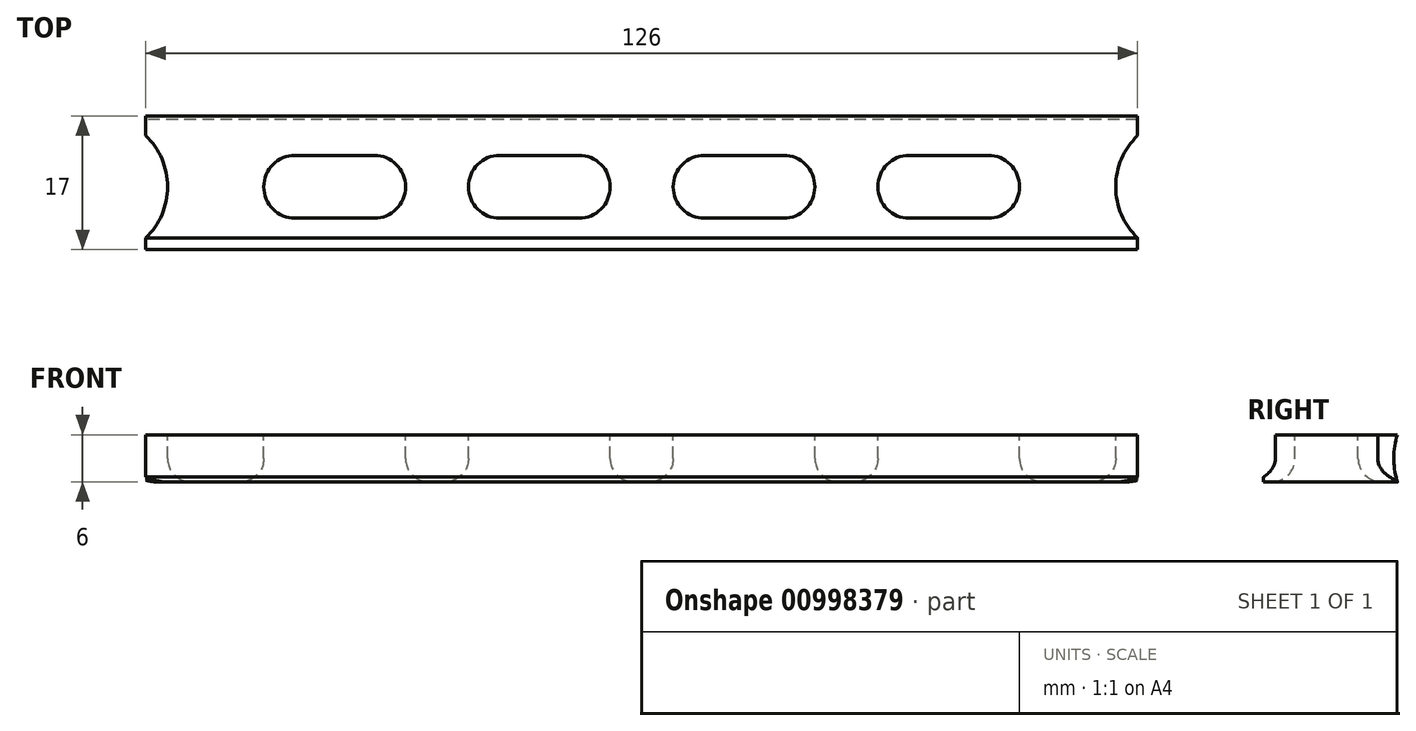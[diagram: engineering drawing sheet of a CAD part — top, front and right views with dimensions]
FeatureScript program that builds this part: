
annotation { "Feature Type Name" : "Feature", "Feature Type Description" : "" }
export const myFeature = defineFeature(function(context is Context, id is Id, definition is map)
    precondition{}
    {
        {
            var Q0;
            Q0=qCreatedBy(makeId("Right.planeOp"),FACE);
            var sketch = newSketch(context, id + "F0", { "sketchPlane" : qUnion([Q0])});
            skLineSegment(sketch, "E0.bottom", {"start": v(0, 0) * mm, "end": v(-17, 0) * mm});
            skLineSegment(sketch, "E0.top", {"start": v(0, 6) * mm, "end": v(-17, 6) * mm});
            skLineSegment(sketch, "E0.right", {"start": v(-17, 0) * mm, "end": v(-17, 6) * mm});
            skArc(sketch, "E1", {"start": v(0, 6) * mm, "mid": v(-0.46, 3) * mm, "end": v(0, 0) * mm});
            skSolve(sketch);
        }
        {
            var Q0;
            Q0=makeQuery(id+"F0.imprint","IMPRINT",FACE,{"disambiguationData":[TD([[makeQuery(id+"F0.imprint","IMPRINT",EDGE,{"derivedFrom":sQuery(id+"F0.wireOp",EDGE,"E0.bottom")}),-1.0]])]});
            extrude(context, id + "F1", {"entities" : qUnion([Q0]), "depth" : 63 * mm, "offsetDistance" : 25 * mm});
        }
        {
            var Q0;
            Q0=makeQuery(id+"F1.opExtrude","SWEPT_FACE",FACE,{"disambiguationData":[OSD([sQuery(id+"F0.wireOp",EDGE,"E0.top")])]});
            var sketch = newSketch(context, id + "F2", { "sketchPlane" : qUnion([Q0])});
            skPoint(sketch, "E2", {"position": v(63, -2.5) * mm});
            skPoint(sketch, "E3", {"position": v(63, -15.5) * mm});
            skArc(sketch, "E4", {"start": v(63, -2.5) * mm, "mid": v(60.22, -9) * mm, "end": v(63, -15.5) * mm});
            skLineSegment(sketch, "E5.bottom", {"start": v(8, -5) * mm, "end": v(18, -5) * mm});
            skLineSegment(sketch, "E5.top", {"start": v(8, -13) * mm, "end": v(18, -13) * mm});
            skArc(sketch, "E6", {"start": v(18, -5) * mm, "mid": v(22, -9) * mm, "end": v(18, -13) * mm});
            skArc(sketch, "E7", {"start": v(8, -5) * mm, "mid": v(4, -9) * mm, "end": v(8, -13) * mm});
            skLineSegment(sketch, "E8.bottom", {"start": v(34, -5) * mm, "end": v(44, -5) * mm});
            skLineSegment(sketch, "E8.top", {"start": v(34, -13) * mm, "end": v(44, -13) * mm});
            skArc(sketch, "E9", {"start": v(44, -5) * mm, "mid": v(48, -9) * mm, "end": v(44, -13) * mm});
            skArc(sketch, "E10", {"start": v(34, -5) * mm, "mid": v(30, -9) * mm, "end": v(34, -13) * mm});
            skSolve(sketch);
        }
        {
            var Q0;
            {var subQ0=sQuery(id+"F2.wireOp",EDGE,"E4");Q0=makeQuery(id+"F2.imprint","IMPRINT",FACE,{"disambiguationData":[TD([[makeQuery(id+"F2.imprint","IMPRINT",EDGE,{"derivedFrom":subQ0}),1.0]])]});}
            var Q1;
            Q1=makeQuery(id+"F2.imprint","IMPRINT",FACE,{"disambiguationData":[TD([[makeQuery(id+"F2.imprint","IMPRINT",EDGE,{"derivedFrom":sQuery(id+"F2.wireOp",EDGE,"E5.bottom")}),-1.0]])]});
            var Q2;
            Q2=makeQuery(id+"F2.imprint","IMPRINT",FACE,{"disambiguationData":[TD([[makeQuery(id+"F2.imprint","IMPRINT",EDGE,{"derivedFrom":sQuery(id+"F2.wireOp",EDGE,"E8.bottom")}),-1.0]])]});
            extrude(context, id + "F3", {"entities" : qUnion([Q0, Q1, Q2]), "operationType" : NewBodyOperationType.REMOVE, "endBound" : BoundingType.THROUGH_ALL, "oppositeDirection" : true, "depth" : 25 * mm, "offsetDistance" : 25 * mm});
        }
        {
            var Q0;
            Q0=makeQuery(id+"F3.boolean.opBoolean","COPY",EDGE,{"derivedFrom":makeQuery(id+"F3.opExtrude","CAP_EDGE",EDGE,{"disambiguationData":[OSD([sQuery(id+"F2.wireOp",EDGE,"E4")])],"isStart":true})});
            var Q1;
            Q1=makeQuery(id+"F3.boolean.opBoolean","INTERSECT",EDGE,{"derivedFrom":[makeQuery(id+"F1.opExtrude","SWEPT_FACE",FACE,{"disambiguationData":[OSD([sQuery(id+"F0.wireOp",EDGE,"E0.bottom")])]}),makeQuery(id+"F3.opExtrude","SWEPT_FACE",FACE,{"disambiguationData":[OSD([sQuery(id+"F2.wireOp",EDGE,"E4")])]})]});
            fillet(context, id + "F4", {"entities" : qUnion([Q0, Q1]), "radius" : 3 * mm, "tangentPropagation" : true, "allowEdgeOverflow" : false});
        }
        {
            var Q0;
            Q0=makeQuery(id+"F3.boolean.opBoolean","COPY",EDGE,{"derivedFrom":makeQuery(id+"F3.opExtrude","CAP_EDGE",EDGE,{"disambiguationData":[OSD([sQuery(id+"F2.wireOp",EDGE,"E8.bottom")])],"isStart":true})});
            var Q1;
            Q1=makeQuery(id+"F3.boolean.opBoolean","COPY",EDGE,{"derivedFrom":makeQuery(id+"F3.opExtrude","CAP_EDGE",EDGE,{"disambiguationData":[OSD([sQuery(id+"F2.wireOp",EDGE,"E5.bottom")])],"isStart":true})});
            var Q2;
            Q2=makeQuery(id+"F3.boolean.opBoolean","INTERSECT",EDGE,{"derivedFrom":[makeQuery(id+"F1.opExtrude","SWEPT_FACE",FACE,{"disambiguationData":[OSD([sQuery(id+"F0.wireOp",EDGE,"E0.bottom")])]}),makeQuery(id+"F3.opExtrude","SWEPT_FACE",FACE,{"disambiguationData":[OSD([sQuery(id+"F2.wireOp",EDGE,"E8.bottom")])]})]});
            var Q3;
            Q3=makeQuery(id+"F3.boolean.opBoolean","INTERSECT",EDGE,{"derivedFrom":[makeQuery(id+"F1.opExtrude","SWEPT_FACE",FACE,{"disambiguationData":[OSD([sQuery(id+"F0.wireOp",EDGE,"E0.bottom")])]}),makeQuery(id+"F3.opExtrude","SWEPT_FACE",FACE,{"disambiguationData":[OSD([sQuery(id+"F2.wireOp",EDGE,"E5.bottom")])]})]});
            fillet(context, id + "F5", {"entities" : qUnion([Q0, Q1, Q2, Q3]), "radius" : 3 * mm, "tangentPropagation" : true, "allowEdgeOverflow" : false});
        }
        {
            var Q0;
            Q0=makeQuery(id+"F1.opExtrude","SWEPT_BODY",BODY,{"disambiguationData":[OSD([sQuery(id+"F0.wireOp",EDGE,"E0.bottom"),sQuery(id+"F0.wireOp",EDGE,"E0.top"),sQuery(id+"F0.wireOp",EDGE,"E0.right"),sQuery(id+"F0.wireOp",EDGE,"6yIWbass-UUZ5-p67e-vw6n-y79Z4zVrPJHl"),sQuery(id+"F0.wireOp",EDGE,"iosmHDo3-xEOO-oSXW-RUBl-dEGRPoRzE2tZ")])]});
            var Q1;
            Q1=makeQuery(id+"F1.opExtrude","CAP_FACE",FACE,{"disambiguationData":[OSD([sQuery(id+"F0.wireOp",EDGE,"E0.bottom"),sQuery(id+"F0.wireOp",EDGE,"E0.top"),sQuery(id+"F0.wireOp",EDGE,"E0.right"),sQuery(id+"F0.wireOp",EDGE,"6yIWbass-UUZ5-p67e-vw6n-y79Z4zVrPJHl"),sQuery(id+"F0.wireOp",EDGE,"iosmHDo3-xEOO-oSXW-RUBl-dEGRPoRzE2tZ")])],"isStart":true});
            mirror(context, id + "F6", {"operationType" : NewBodyOperationType.ADD, "entities" : qUnion([Q0]), "mirrorPlane" : qUnion([Q1])});
        }
        {
            var Q0;
            {var subQ0=sQuery(id+"F0.wireOp",EDGE,"E0.bottom");var subQ1=sQuery(id+"F0.wireOp",EDGE,"E0.top");var subQ2=sQuery(id+"F0.wireOp",EDGE,"E0.right");Q0=makeQuery(id+"F6.opPattern","COPY",FACE,{"derivedFrom":makeQuery(id+"F3.boolean.opBoolean","SPLIT",FACE,{"disambiguationData":[TD([makeQuery(id+"F1.opExtrude","SWEPT_FACE",FACE,{"disambiguationData":[OSD([subQ2])]})])],"derivedFrom":makeQuery(id+"F1.opExtrude","CAP_FACE",FACE,{"disambiguationData":[OSD([subQ0,subQ1,subQ2,sQuery(id+"F0.wireOp",EDGE,"6yIWbass-UUZ5-p67e-vw6n-y79Z4zVrPJHl"),sQuery(id+"F0.wireOp",EDGE,"iosmHDo3-xEOO-oSXW-RUBl-dEGRPoRzE2tZ")])],"isStart":false})}),"instanceName":"1"});}
            extrude(context, id + "F7", {"entities" : qUnion([Q0]), "operationType" : NewBodyOperationType.REMOVE, "endBound" : BoundingType.THROUGH_ALL, "oppositeDirection" : true, "depth" : 25 * mm, "offsetDistance" : 25 * mm});
        }
    });
